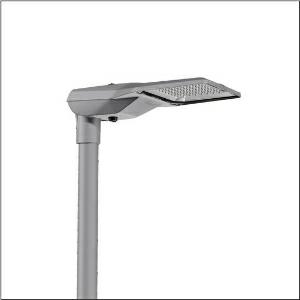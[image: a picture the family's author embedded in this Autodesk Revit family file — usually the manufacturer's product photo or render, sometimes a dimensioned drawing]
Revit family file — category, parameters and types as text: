
# Revit family: streetlight_sl_21_iq_midi___st0_8a_5xe3c31y08mb_7afc
name_source: partatom
category: Lighting Fixtures
units: mm (PartAtom-declared; Revit-internal decimal feet)

## family parameters
Cut with Voids When Loaded = No
Host = Face
Light Source = No
Part Type = Normal
Room Calculation Point = No
Round Connector Dimension = Use Diameter
Shared = No

## types (1)
- --- (1 x LED, 18340 lm, 129.3 W, 3000K)
    Apparent Load = 129 VA
    CIE Flux Codes = 38 75 97 100 100
    Color Rendering = 70
    Color Temperature = 3000K
    Default Elevation = 1800 mm
    Description = Streetlight SL 21 iQ midi, mast luminaire, primary light control with lens, of PMMA, primary optical cover: cover, of toughened safety glass, transparent, light distribution: ST0.8a, light emission: direct distribution, primary light characteristic: asymmetric, installation type: post-top, side-entry, LED, High Power LED, rated luminous flux: 18.340lm, luminous efficacy: 142lm/W, light colour: 730, colour temperature: 3000K, control gear: iQ-Street Remote, D4i with power reduction, control: pre-setting: logarithmic dimming characteristic, Street-Remote, Auto-Match, Temp-Guard, Lumen-Switch, Night-Set, Smart-Wire, Light-Fading, Desk-Remote (wireless, voltage-free reading and setting of iQ features in the workshop via application-optimized NFC function/RFID function), optimised constant luminous flux control (CLO 2.0), mains connection: 230..240V, AC, 50/60Hz, start of lifetime: 129W, end of service life: 142W, reduction: 56W, luminaire housing, of diecast aluminium, powder-coated, Siteco® metallic grey (DB 702S), corrosivity category C5 mid according to DIN EN ISO 12944, please order mast flange separately, inclination adjustable: 0°, 5°, 10°, 15°, sealing non-destructively replaceable, multi-level sealing system, length: 644mm, width: 335mm, height: 110mm, mast flange for spigot size: 42mm (side-entry): 5XC10008XM4, 60/48mm (side-entry/post-top): 5XC10108XM2, 76/60mm (side-entry/post-top): 5XC10108XM1, mounting height: 4..8m, Smart Interface below and above, protection rating (complete): IP66, insulation class (complete): insulation class II (safety insulation), certification: CE, ENEC, ENEC+, VDE, impact resistance: IK10, permissible operating ambient temperature for outdoor applications: -40..+50°C, standard-compliant lighting for roads and squares, packaging unit: 1 piece

Light Distribution: ST0.8a
    Height = 111 mm
    Lamp = 1 x LED
    Lamp Light Flux = 18340 lm
    Lamp Power = 129.3 W
    Lamp count = 1
    Length = 644 mm
    Luminous efficacy = 142 lm/W
    Manufacturer = Siteco
    ModVariant = No
    Model = 5XE3C31Y08MB
    Number of Poles = 1
    OnlyDefault = Yes
    Power Factor = 1
    Product Name = Streetlight SL 21 iQ midi | ST0.8a
    Product group = mast luminaire | pylon top
    ProductGroupID = 6100
    Protection Class = Protection class II
    Protection Degree = IP 66
    RLX_Detail_Level = 1
    RLX_Emergency_Light_Flux = 0 lm
    RLX_Emergency_Type = 0
    RLX_Emergency_Type_DB = No
    RlxData = <blob elided: 27357 chars, md5=433ba16c>
    Socket = socket
    Standby Power = 0 W
    System Light Flux = 18340 lm
    System Power = 129 W
    Type Comments = factory setting: luminous flux: 100 % | dim-lin: 254 | 672 mA
    Type Image = l_1004304.jpg
    URL = http://relux.com
    VarID = @adj_113270
    Voltage = 0 V
    Weight = 0.00 kg
    Width = 336 mm

## geometry (parser evidence)
native form markers: Blend x4, Sweep x11
no freeform markers — native parametric forms only
